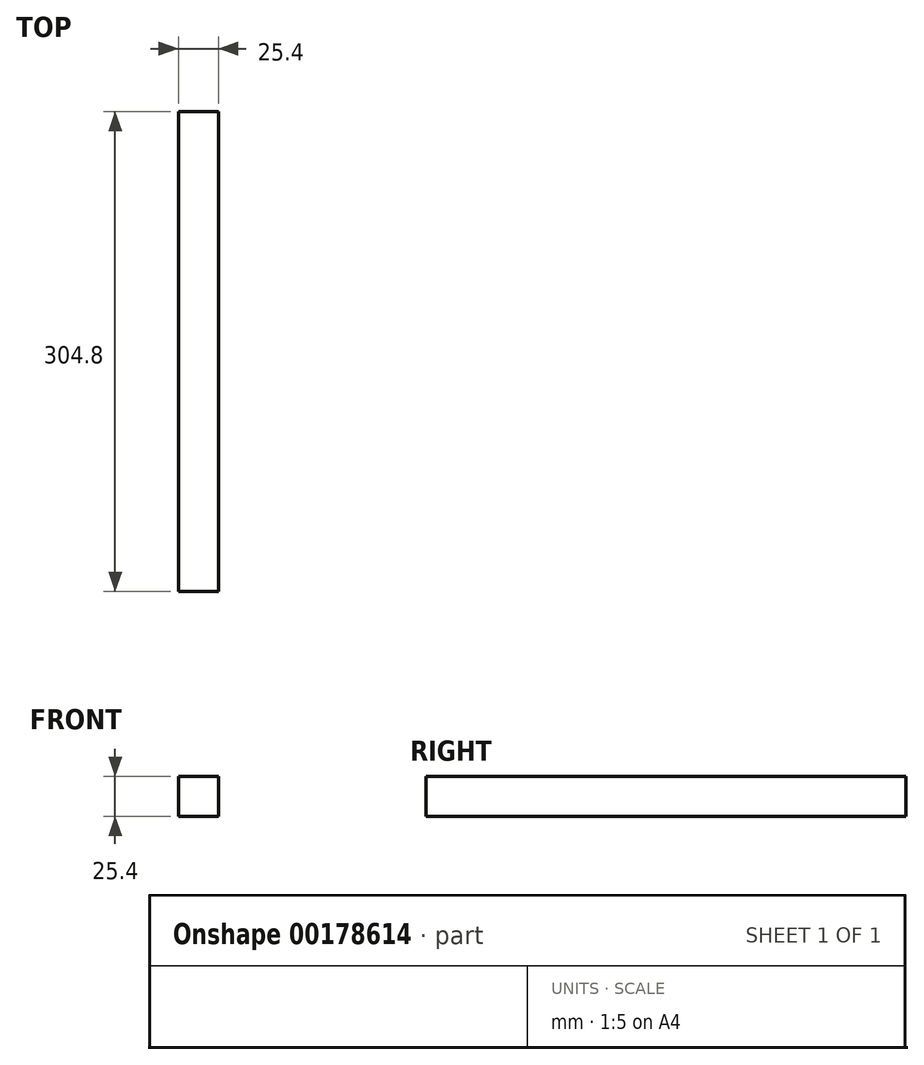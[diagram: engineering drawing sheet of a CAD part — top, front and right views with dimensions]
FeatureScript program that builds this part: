
annotation { "Feature Type Name" : "Feature", "Feature Type Description" : "" }
export const myFeature = defineFeature(function(context is Context, id is Id, definition is map)
    precondition{}
    {
        {
            var Q0;
            Q0=qCreatedBy(makeId("Front.planeOp"),FACE);
            var sketch = newSketch(context, id + "F0", { "sketchPlane" : qUnion([Q0])});
            skLineSegment(sketch, "E0.bottom", {"start": v(0, 0) * mm, "end": v(25.4, 0) * mm});
            skLineSegment(sketch, "E0.top", {"start": v(0, 25.4) * mm, "end": v(25.4, 25.4) * mm});
            skLineSegment(sketch, "E0.left", {"start": v(0, 0) * mm, "end": v(0, 25.4) * mm});
            skLineSegment(sketch, "E0.right", {"start": v(25.4, 0) * mm, "end": v(25.4, 25.4) * mm});
            skSolve(sketch);
        }
        {
            var Q0;
            Q0 = qSketchRegion(id + "F0", true);
            extrude(context, id + "F1", {"entities" : qUnion([Q0]), "endBound" : BoundingType.SYMMETRIC, "depth" : 304.8 * mm});
        }
    });
